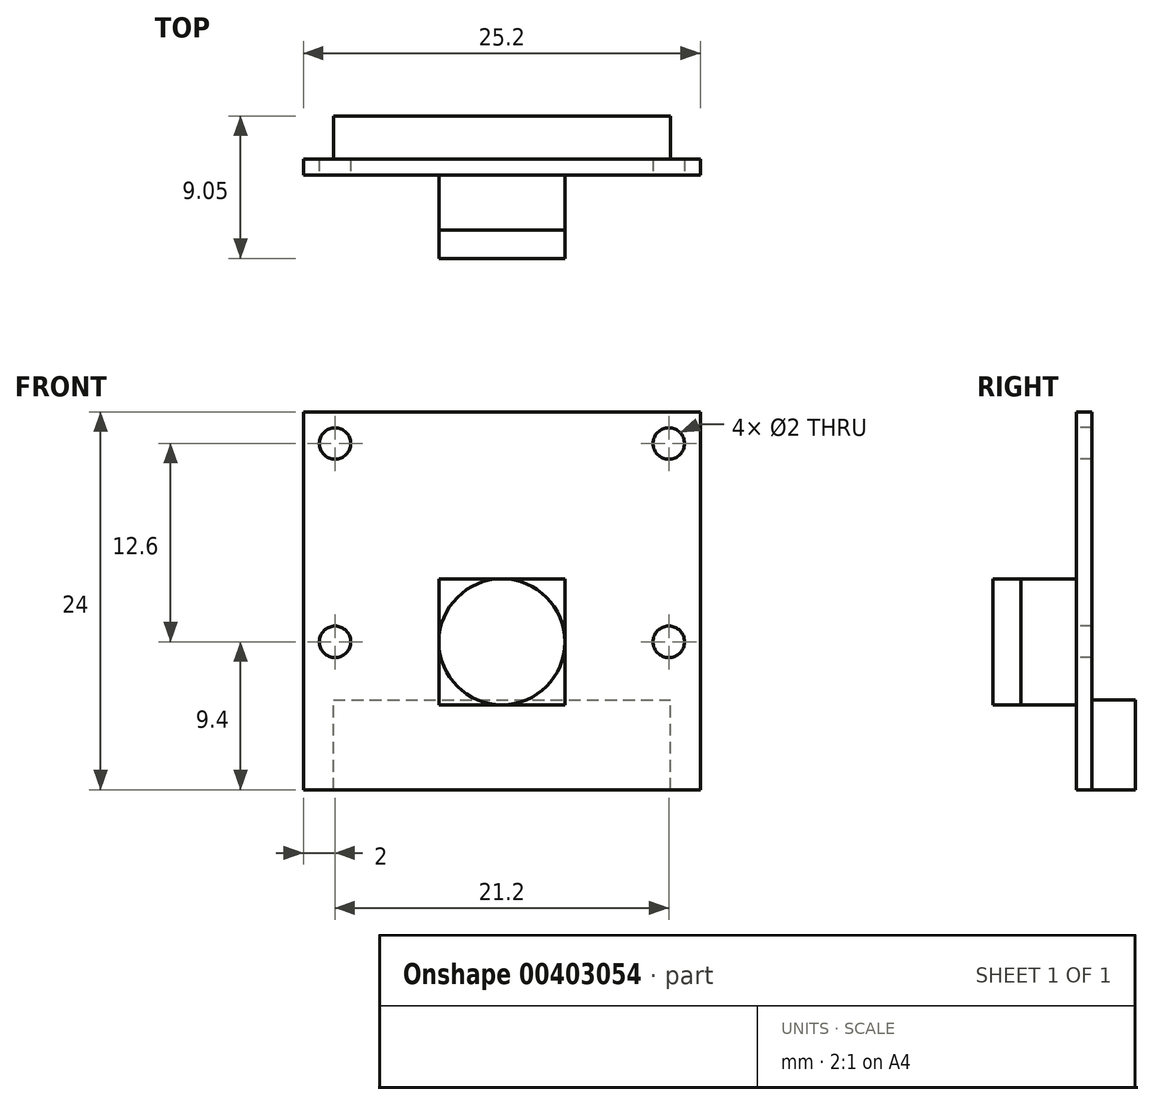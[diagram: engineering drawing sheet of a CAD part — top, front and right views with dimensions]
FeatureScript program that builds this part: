
annotation { "Feature Type Name" : "Feature", "Feature Type Description" : "" }
export const myFeature = defineFeature(function(context is Context, id is Id, definition is map)
    precondition{}
    {
        {
            var Q0;
            Q0=qCreatedBy(makeId("Front.planeOp"),FACE);
            var sketch = newSketch(context, id + "F0", { "sketchPlane" : qUnion([Q0])});
            skLineSegment(sketch, "E0.bottom", {"start": v(12.6, -12) * mm, "end": v(-12.6, -12) * mm});
            skLineSegment(sketch, "E0.top", {"start": v(12.6, 12) * mm, "end": v(-12.6, 12) * mm});
            skLineSegment(sketch, "E0.left", {"start": v(12.6, -12) * mm, "end": v(12.6, 12) * mm});
            skLineSegment(sketch, "E0.right", {"start": v(-12.6, -12) * mm, "end": v(-12.6, 12) * mm});
            skPoint(sketch, "E0.middle", {"position": v(0, 0) * mm});
            skCircle(sketch, "E1", {"center": v(-10.6, 10) * mm, "radius": 1 * mm});
            skCircle(sketch, "E2", {"center": v(10.6, 10) * mm, "radius": 1 * mm});
            skCircle(sketch, "E3", {"center": v(-10.6, -2.6) * mm, "radius": 1 * mm});
            skCircle(sketch, "E4", {"center": v(10.6, -2.6) * mm, "radius": 1 * mm});
            skLineSegment(sketch, "E5.bottom", {"start": v(-10.6, 10) * mm, "end": v(10.6, 10) * mm, "construction": true});
            skLineSegment(sketch, "E5.top", {"start": v(-10.6, -2.6) * mm, "end": v(10.6, -2.6) * mm, "construction": true});
            skLineSegment(sketch, "E5.left", {"start": v(-10.6, 10) * mm, "end": v(-10.6, -2.6) * mm, "construction": true});
            skLineSegment(sketch, "E5.right", {"start": v(10.6, 10) * mm, "end": v(10.6, -2.6) * mm, "construction": true});
            skPoint(sketch, "E6.middle", {"position": v(0, -2.6) * mm});
            skSolve(sketch);
        }
        {
            var Q0;
            Q0=makeQuery(id+"F0.imprint","IMPRINT",FACE,{"disambiguationData":[TD([[makeQuery(id+"F0.imprint","IMPRINT",EDGE,{"derivedFrom":sQuery(id+"F0.wireOp",EDGE,"E0.bottom")}),-1.0]])]});
            var sketch = newSketch(context, id + "F1", { "sketchPlane" : qUnion([Q0])});
            skPoint(sketch, "E7.0", {"position": v(0, -2.6) * mm});
            skLineSegment(sketch, "E8.bottom", {"start": v(4, -6.6) * mm, "end": v(-4, -6.6) * mm});
            skLineSegment(sketch, "E8.top", {"start": v(4, 1.4) * mm, "end": v(-4, 1.4) * mm});
            skLineSegment(sketch, "E8.left", {"start": v(4, -6.6) * mm, "end": v(4, 1.4) * mm});
            skLineSegment(sketch, "E8.right", {"start": v(-4, -6.6) * mm, "end": v(-4, 1.4) * mm});
            skCircle(sketch, "E9", {"center": v(0, -2.6) * mm, "radius": 4 * mm});
            skSolve(sketch);
        }
        {
            var Q0;
            Q0=makeQuery(id+"F0.imprint","IMPRINT",FACE,{"disambiguationData":[TD([[makeQuery(id+"F0.imprint","IMPRINT",EDGE,{"derivedFrom":sQuery(id+"F0.wireOp",EDGE,"E0.bottom")}),-1.0]])]});
            var sketch = newSketch(context, id + "F2", { "sketchPlane" : qUnion([Q0])});
            skLineSegment(sketch, "E10.bottom", {"start": v(-10.7, -12) * mm, "end": v(10.7, -12) * mm});
            skLineSegment(sketch, "E10.top", {"start": v(-10.7, -6.3) * mm, "end": v(10.7, -6.3) * mm});
            skLineSegment(sketch, "E10.left", {"start": v(-10.7, -12) * mm, "end": v(-10.7, -6.3) * mm});
            skLineSegment(sketch, "E10.right", {"start": v(10.7, -12) * mm, "end": v(10.7, -6.3) * mm});
            skPoint(sketch, "E10.middle", {"position": v(0, -9.15) * mm});
            skSolve(sketch);
        }
        {
            var Q0;
            Q0=makeQuery(id+"F0.imprint","IMPRINT",FACE,{"disambiguationData":[TD([[makeQuery(id+"F0.imprint","IMPRINT",EDGE,{"derivedFrom":sQuery(id+"F0.wireOp",EDGE,"E0.bottom")}),-1.0]])]});
            extrude(context, id + "F3", {"entities" : qUnion([Q0]), "oppositeDirection" : true, "depth" : 1 * mm});
        }
        {
            var Q0;
            Q0 = qSketchRegion(id + "F1", true);
            extrude(context, id + "F4", {"entities" : qUnion([Q0]), "operationType" : NewBodyOperationType.ADD, "depth" : 3.5 * mm});
        }
        {
            var Q0;
            {var subQ0=sQuery(id+"F1.wireOp",EDGE,"E9");var subQ1=makeQuery(id+"F1.imprint","INTERSECT",VERTEX,{"derivedFrom":[sQuery(id+"F1.wireOp",EDGE,"E8.top"),subQ0]});Q0=makeQuery(id+"F1.imprint","IMPRINT",FACE,{"disambiguationData":[TD([[makeQuery(id+"F1.imprint","IMPRINT",EDGE,{"disambiguationData":[TD([[subQ1,1.0]])],"derivedFrom":subQ0}),1.0]])]});}
            extrude(context, id + "F5", {"entities" : qUnion([Q0]), "operationType" : NewBodyOperationType.ADD, "depth" : 5.3 * mm});
        }
        {
            var Q0;
            Q0=makeQuery(id+"F2.imprint","IMPRINT",FACE,{"disambiguationData":[TD([[makeQuery(id+"F2.imprint","IMPRINT",EDGE,{"derivedFrom":sQuery(id+"F2.wireOp",EDGE,"E10.bottom")}),-1.0]])]});
            extrude(context, id + "F6", {"entities" : qUnion([Q0]), "operationType" : NewBodyOperationType.ADD, "oppositeDirection" : true, "depth" : 3.75 * mm});
        }
    });
